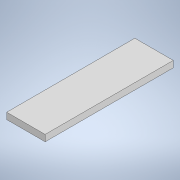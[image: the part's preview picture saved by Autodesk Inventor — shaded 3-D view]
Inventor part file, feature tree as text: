
AUTODESK INVENTOR PART (.ipt)
format: ipt  version: 2020 (Build 240168000, 168)  size: 90,112 bytes
history: native  units: mm
features: extrude x1, sketch x1
ambient origin geometry x8: Origin, YZ Plane, XZ Plane, XY Plane, X Axis, Y Axis, Z Axis, Center Point
bodies: Solid1 (feature_tree)
feature tree (2):
  extrude  "Extrusion1"  Depth=25.0mm
  sketch  "Sketch1"  dims[d0=150.0mm d1=25.0mm d2=500.0mm d3=0.0mm]
